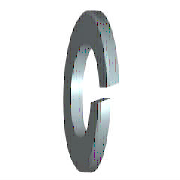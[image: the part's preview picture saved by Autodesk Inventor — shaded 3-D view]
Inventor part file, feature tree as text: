
AUTODESK INVENTOR PART (.ipt)
format: ipt  version: 2021 (Build 250183000, 183)  size: 126,464 bytes
history: native  units: mm (DEFAULTED — no unit token found)
features: sketch x2, extrude x1, other x1, plane x1
ambient origin geometry x6: Origin, YZ Plane, X Axis, Y Axis, Z Axis, Center Point
bodies: Solid1 (feature_tree), Body (feature_tree)
feature tree (5):
  extrude  "Cut"  Depth=24.1mm
  other  "Work Axis1"
  plane  "Work Plane1"
  sketch  "Sketch1"  dims[d0=14.2mm d1=24.1mm]
  sketch  "Sketch2"  dims[d2=3.15mm d3=0.0mm d4=0.63mm d5=0.63mm d6=12.217305mm d7=3.15mm d8=0.0mm d9=0.0mm d10=0.0mm d11=0.0mm d12=0.0mm]
